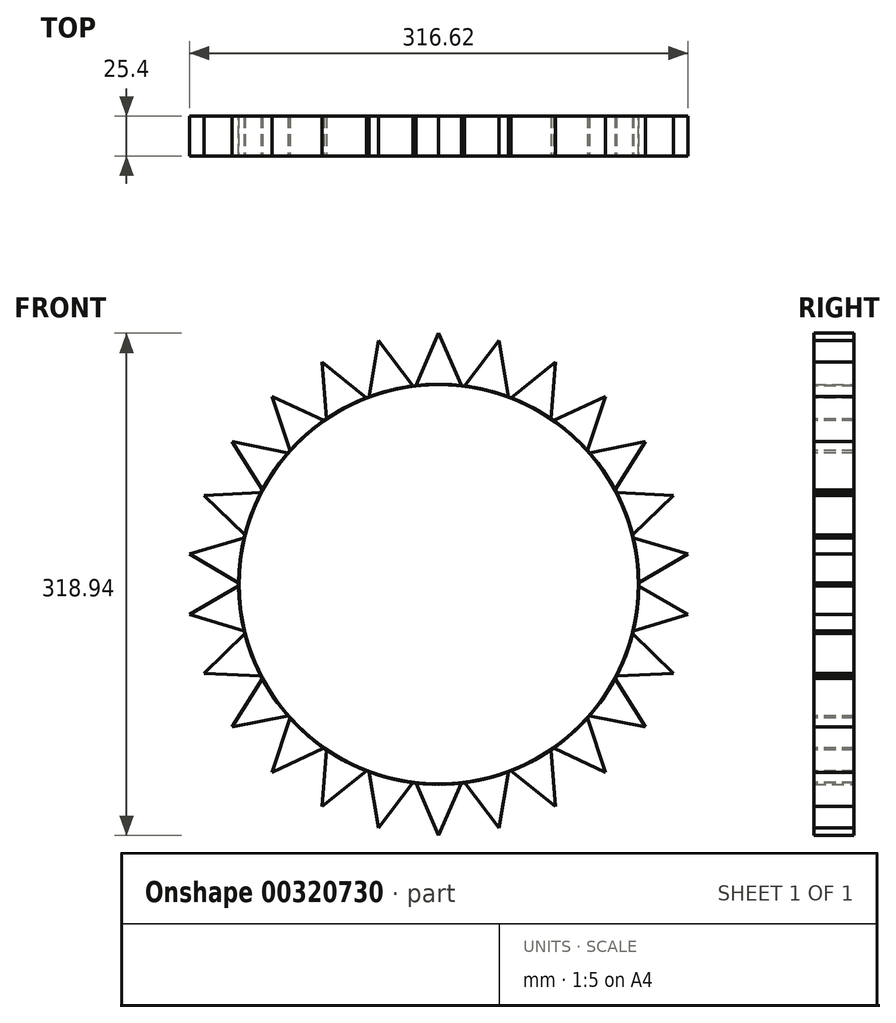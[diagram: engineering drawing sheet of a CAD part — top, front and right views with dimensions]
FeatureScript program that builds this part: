
annotation { "Feature Type Name" : "Feature", "Feature Type Description" : "" }
export const myFeature = defineFeature(function(context is Context, id is Id, definition is map)
    precondition{}
    {
        {
            var Q0;
            Q0=qCreatedBy(makeId("Front.planeOp"),FACE);
            var sketch = newSketch(context, id + "F0", { "sketchPlane" : qUnion([Q0])});
            skCircle(sketch, "E0", {"center": v(0, 0) * mm, "radius": 127 * mm});
            skSolve(sketch);
        }
        {
            var Q0;
            Q0=makeQuery(id+"F0.imprint","IMPRINT",FACE,{"disambiguationData":[TD([[makeQuery(id+"F0.imprint","IMPRINT",EDGE,{"derivedFrom":sQuery(id+"F0.wireOp",EDGE,"E0")}),1.0]])]});
            extrude(context, id + "F1", {"entities" : qUnion([Q0]), "depth" : 25.4 * mm, "symmetric" : true});
        }
        {
            var Q0;
            Q0=makeQuery(id+"F1.opExtrude","CAP_FACE",FACE,{"disambiguationData":[OSD([sQuery(id+"F0.wireOp",EDGE,"E0")])],"isStart":false});
            var sketch = newSketch(context, id + "F2", { "sketchPlane" : qUnion([Q0])});
            skLineSegment(sketch, "E1", {"start": v(-14.4, 126.18) * mm, "end": v(0, 159.47) * mm});
            skLineSegment(sketch, "E2", {"start": v(0, 159.47) * mm, "end": v(14.4, 126.18) * mm});
            skArc(sketch, "E3.0", {"start": v(14.4, 126.18) * mm, "mid": v(0, 127) * mm, "end": v(-14.4, 126.18) * mm});
            skSolve(sketch);
        }
        {
            var Q0;
            Q0 = qSketchRegion(id + "F2", true);
            var Q1;
            Q1=makeQuery(id+"F1.opExtrude","CAP_FACE",FACE,{"disambiguationData":[OSD([sQuery(id+"F0.wireOp",EDGE,"E0")])],"isStart":true});
            extrude(context, id + "F3", {"entities" : qUnion([Q0]), "operationType" : NewBodyOperationType.ADD, "endBound" : BoundingType.UP_TO_SURFACE, "oppositeDirection" : true, "endBoundEntityFace" : qUnion([Q1]), "depth" : 25.4 * mm});
        }
        {
            var Q0;
            Q0=makeQuery(id+"F1.opExtrude","SWEPT_BODY",BODY,{"disambiguationData":[OSD([sQuery(id+"F0.wireOp",EDGE,"E0")])]});
            var Q1;
            Q1=makeQuery(id+"F1.opExtrude","SWEPT_FACE",FACE,{"disambiguationData":[OSD([sQuery(id+"F0.wireOp",EDGE,"E0")])]});
            circularPattern(context, id + "F4", {"entities" : qUnion([Q0]), "axis" : qUnion([Q1]), "angle" : 360 * degree, "instanceCount" : 26, "equalSpace" : true});
        }
    });
